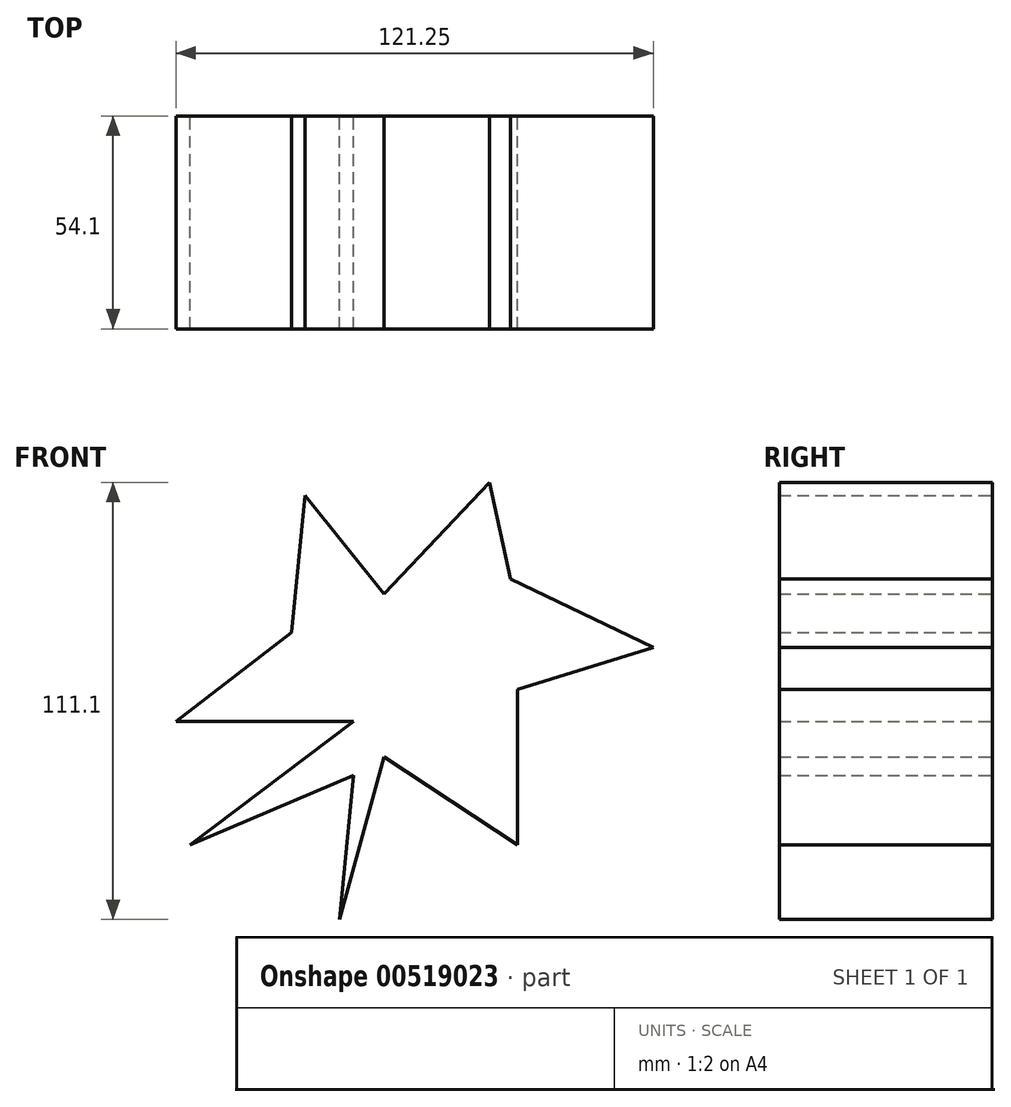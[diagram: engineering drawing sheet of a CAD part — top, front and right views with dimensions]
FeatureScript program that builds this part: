
annotation { "Feature Type Name" : "Feature", "Feature Type Description" : "" }
export const myFeature = defineFeature(function(context is Context, id is Id, definition is map)
    precondition{}
    {
        {
            var Q0;
            Q0=qCreatedBy(makeId("Front.planeOp"),FACE);
            var sketch = newSketch(context, id + "F0", { "sketchPlane" : qUnion([Q0])});
            skLineSegment(sketch, "E0", {"start": v(0, 0) * mm, "end": v(11.28, 41.33) * mm});
            skLineSegment(sketch, "E1", {"start": v(11.28, 41.33) * mm, "end": v(45.12, 19.02) * mm});
            skLineSegment(sketch, "E2", {"start": v(45.12, 19.02) * mm, "end": v(45.12, 58.54) * mm});
            skLineSegment(sketch, "E3", {"start": v(45.12, 58.54) * mm, "end": v(79.66, 69.17) * mm});
            skLineSegment(sketch, "E4", {"start": v(43.36, 86.54) * mm, "end": v(38.07, 111.1) * mm});
            skLineSegment(sketch, "E5", {"start": v(38.07, 111.1) * mm, "end": v(11.28, 82.72) * mm});
            skLineSegment(sketch, "E6", {"start": v(11.28, 82.72) * mm, "end": v(-8.84, 107.75) * mm});
            skLineSegment(sketch, "E7", {"start": v(-41.6, 50.38) * mm, "end": v(3.52, 50.38) * mm});
            skLineSegment(sketch, "E8", {"start": v(-38.07, 19.02) * mm, "end": v(3.52, 36.62) * mm});
            skLineSegment(sketch, "E9", {"start": v(3.52, 36.62) * mm, "end": v(0, 0) * mm});
            skLineSegment(sketch, "E10", {"start": v(-8.84, 107.75) * mm, "end": v(-12.2, 72.95) * mm});
            skLineSegment(sketch, "E11", {"start": v(-12.2, 72.95) * mm, "end": v(-41.6, 50.38) * mm});
            skLineSegment(sketch, "E12", {"start": v(43.36, 86.54) * mm, "end": v(79.66, 69.17) * mm});
            skLineSegment(sketch, "E13", {"start": v(3.52, 50.38) * mm, "end": v(-38.07, 19.02) * mm});
            skSolve(sketch);
        }
        {
            var Q0;
            Q0 = qSketchRegion(id + "F0", true);
            extrude(context, id + "F1", {"entities" : qUnion([Q0]), "endBound" : BoundingType.SYMMETRIC, "depth" : 54.1 * mm, "offsetDistance" : 25.4 * mm});
        }
    });
